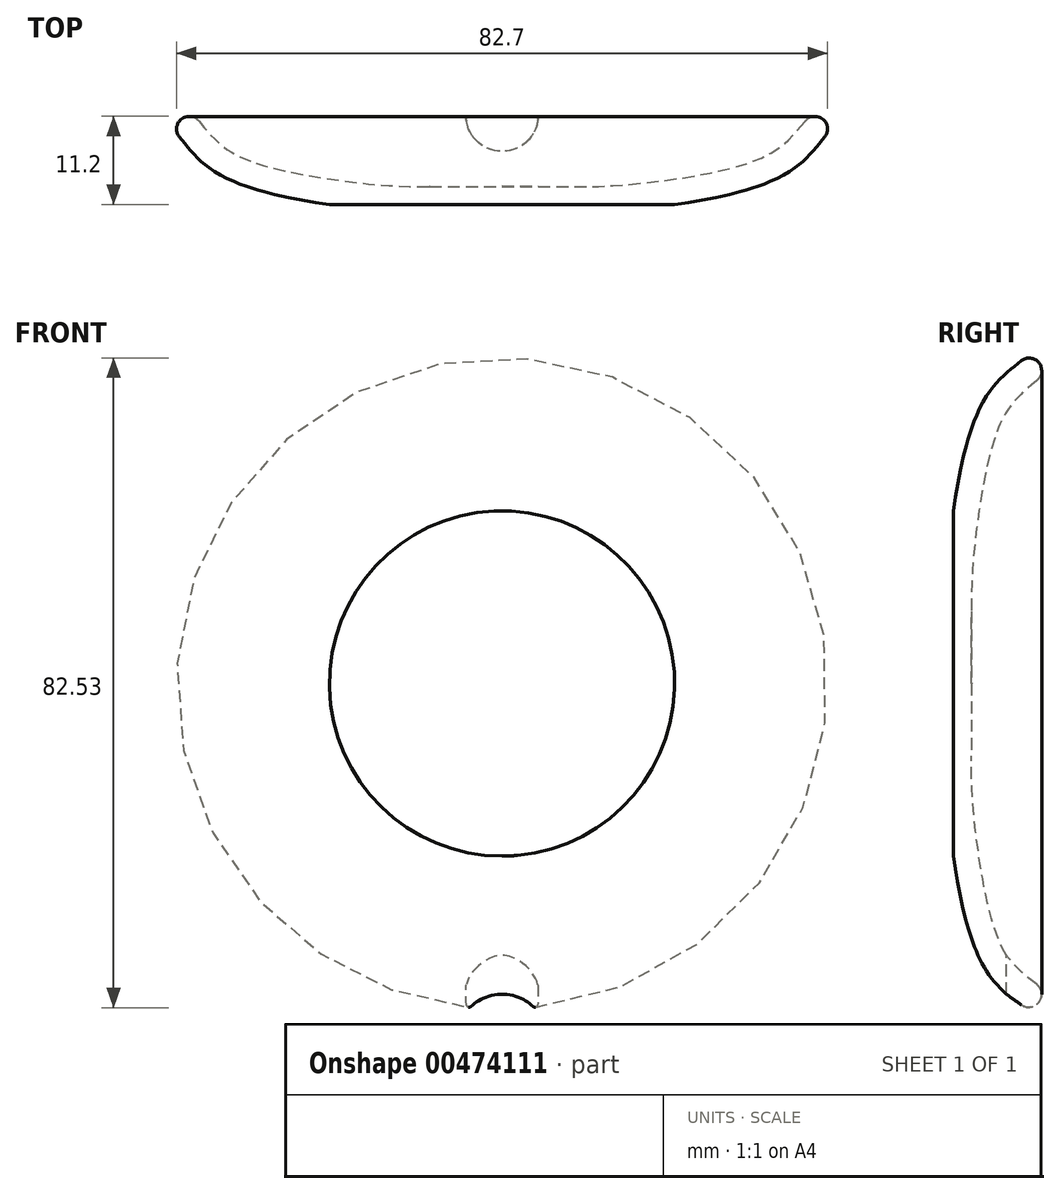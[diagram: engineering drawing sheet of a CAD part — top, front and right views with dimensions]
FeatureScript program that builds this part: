
annotation { "Feature Type Name" : "Feature", "Feature Type Description" : "" }
export const myFeature = defineFeature(function(context is Context, id is Id, definition is map)
    precondition{}
    {
        {
            var Q0;
            Q0=qCreatedBy(makeId("Top.planeOp"),FACE);
            var sketch = newSketch(context, id + "F0", { "sketchPlane" : qUnion([Q0])});
            skLineSegment(sketch, "E0", {"start": v(0, 0) * mm, "end": v(0, 3.18) * mm});
            skFitSpline(sketch, "E1", {"points": [v(0, 3.17) * mm, v(13.71, 3.18) * mm, v(31, 5.97) * mm, v(38.51, 11.39) * mm], "startDerivative": vector(47.35, 0) * mm, "endDerivative": vector(25.98, 33.1) * mm});
            skFitSpline(sketch, "E2.0", {"points": [v(0, 0) * mm, v(1.93, 0) * mm, v(4.47, -0.06) * mm, v(7.68, -0.12) * mm, v(10.12, -0.13) * mm, v(12.27, -0.08) * mm, v(14.1, 0.01) * mm, v(16.04, 0.15) * mm, v(18.57, 0.38) * mm, v(21.71, 0.77) * mm, v(24.84, 1.26) * mm, v(27.84, 1.84) * mm, v(30.17, 2.4) * mm, v(31.87, 2.91) * mm, v(33.08, 3.32) * mm, v(34.23, 3.79) * mm, v(35.7, 4.5) * mm, v(37.42, 5.62) * mm, v(39.27, 7.32) * mm, v(40.42, 8.68) * mm, v(41, 9.43) * mm]});
            skArc(sketch, "E3", {"start": v(41, 9.43) * mm, "mid": v(40.74, 11.66) * mm, "end": v(38.51, 11.39) * mm});
            skSolve(sketch);
        }
        {
            var Q0;
            Q0=makeQuery(id+"F0.imprint","IMPRINT",FACE,{"disambiguationData":[TD([[makeQuery(id+"F0.imprint","IMPRINT",EDGE,{"derivedFrom":sQuery(id+"F0.wireOp",EDGE,"E0")}),-1.0]])]});
            var Q1;
            Q1=sQuery(id+"F0.wireOp",EDGE,"E0");
            revolve(context, id + "F1", {"entities" : qUnion([Q0]), "axis" : qUnion([Q1]), "revolveType" : RevolveType.FULL});
        }
        {
            var Q0;
            Q0=qCreatedBy(makeId("Front.planeOp"),FACE);
            var sketch = newSketch(context, id + "F2", { "sketchPlane" : qUnion([Q0])});
            skCircle(sketch, "E4", {"center": v(0, 0) * mm, "radius": 133.05 * mm});
            skSolve(sketch);
        }
        {
            var Q0;
            Q0=makeQuery(id+"F2.imprint","IMPRINT",FACE,{"disambiguationData":[TD([[makeQuery(id+"F2.imprint","IMPRINT",EDGE,{"derivedFrom":sQuery(id+"F2.wireOp",EDGE,"E4")}),1.0]])]});
            extrude(context, id + "F3", {"entities" : qUnion([Q0]), "operationType" : NewBodyOperationType.REMOVE, "endBound" : BoundingType.SYMMETRIC, "oppositeDirection" : true, "depth" : 1.6 * mm});
        }
        {
            var Q0;
            Q0=qCreatedBy(makeId("Top.planeOp"),FACE);
            var sketch = newSketch(context, id + "F4", { "sketchPlane" : qUnion([Q0])});
            skCircle(sketch, "E5", {"center": v(0, 12.13) * mm, "radius": 4.59 * mm});
            skLineSegment(sketch, "E6", {"start": v(0, 0) * mm, "end": v(0, 53) * mm});
            skSolve(sketch);
        }
        {
            var Q0;
            Q0=makeQuery(id+"F4.imprint","IMPRINT",FACE,{"disambiguationData":[TD([[makeQuery(id+"F4.imprint","IMPRINT",EDGE,{"derivedFrom":sQuery(id+"F4.wireOp",EDGE,"E5")}),1.0]])]});
            extrude(context, id + "F5", {"entities" : qUnion([Q0]), "operationType" : NewBodyOperationType.REMOVE, "oppositeDirection" : true, "depth" : 61.2 * mm});
        }
    });
